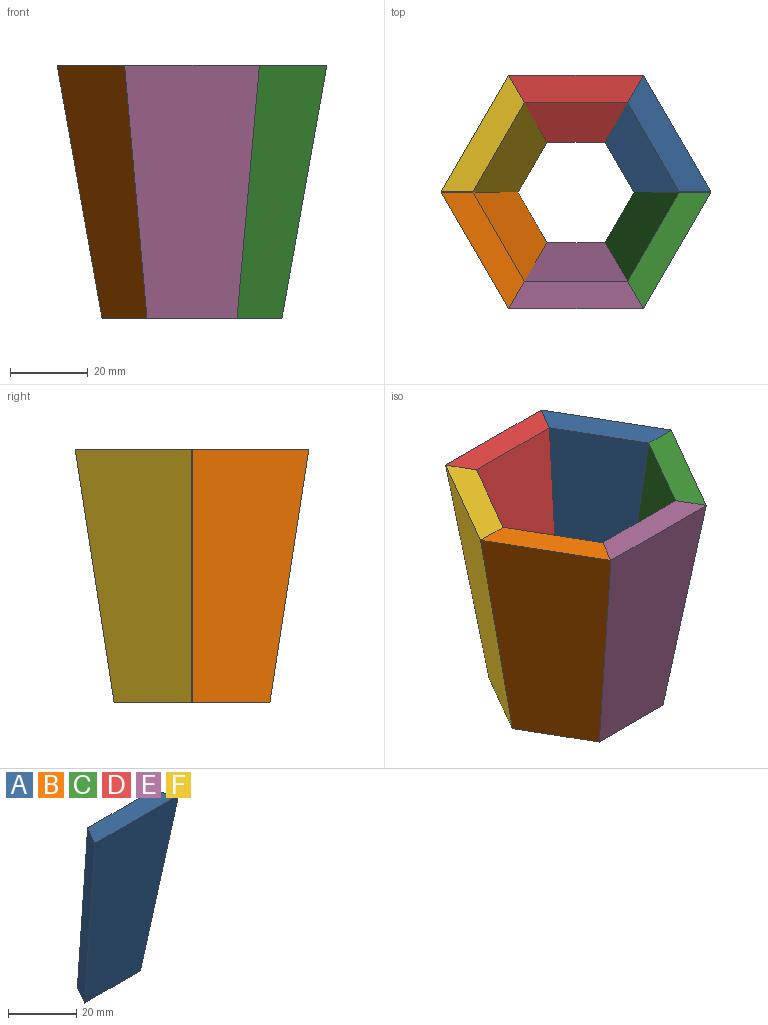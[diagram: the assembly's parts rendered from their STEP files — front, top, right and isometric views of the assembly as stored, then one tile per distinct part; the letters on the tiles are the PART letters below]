
ASSEMBLY  parts=6 mates=5
PART A: 6 faces, bbox 34.6x17.1x65 mm
  f0: plane 65x17.08mm, normal (-0.87,0.5,0), area 531.6mm2, adj f1,f2,f3,f4
  f1: plane 23.09x7.08mm, normal (0,0,-1), area 134.6mm2, adj f0,f3,f4,f5
  f2: plane 34.64x7.08mm, normal (0,0,1), area 216.4mm2, adj f0,f3,f4,f5
  f3: plane 65x34.64mm, normal (0,-0.99,-0.15), area 1898.5mm2, adj f0,f1,f2,f5
  f4: plane 65x26.46mm, normal (0,0.99,0.15), area 1360.6mm2, adj f0,f1,f2,f5
  f5: plane 65x17.08mm, normal (0.87,0.5,0), area 531.6mm2, adj f1,f2,f3,f4
PART B: same geometry as A
PART C: same geometry as A
PART D: same geometry as A
PART E: same geometry as A
PART F: same geometry as A
PLACE A rot(axis=(0,0,1),120deg) t=(24.78,0,32.5)mm
PLACE B rot(axis=(0,0,-1),60deg) t=(24.78,0,32.5)mm
PLACE C rot(axis=(0,0,1),60deg) t=(24.78,0,32.5)mm
PLACE D rot(axis=(0,0,-1),180deg) t=(24.78,0,32.5)mm
PLACE E t=(24.78,0,32.5)mm
PLACE F rot(axis=(0,0,-1),120deg) t=(24.78,0,32.5)mm
MATE fastened A.f0 <-> C.f5  axis (0,-1,0) through (49.56,0,0)mm
MATE fastened F.f0 <-> D.f5  axis (0.87,0.5,0) through (12.39,21.46,0)mm
MATE fastened E.f0 <-> B.f5  axis (-0.87,0.5,0) through (12.39,-21.46,0)mm
MATE fastened B.f0 <-> F.f5  axis (0,1,0) through (0,0,0)mm
MATE fastened E.f5 <-> C.f0  axis (0.87,0.5,0) through (37.17,-21.46,0)mm
